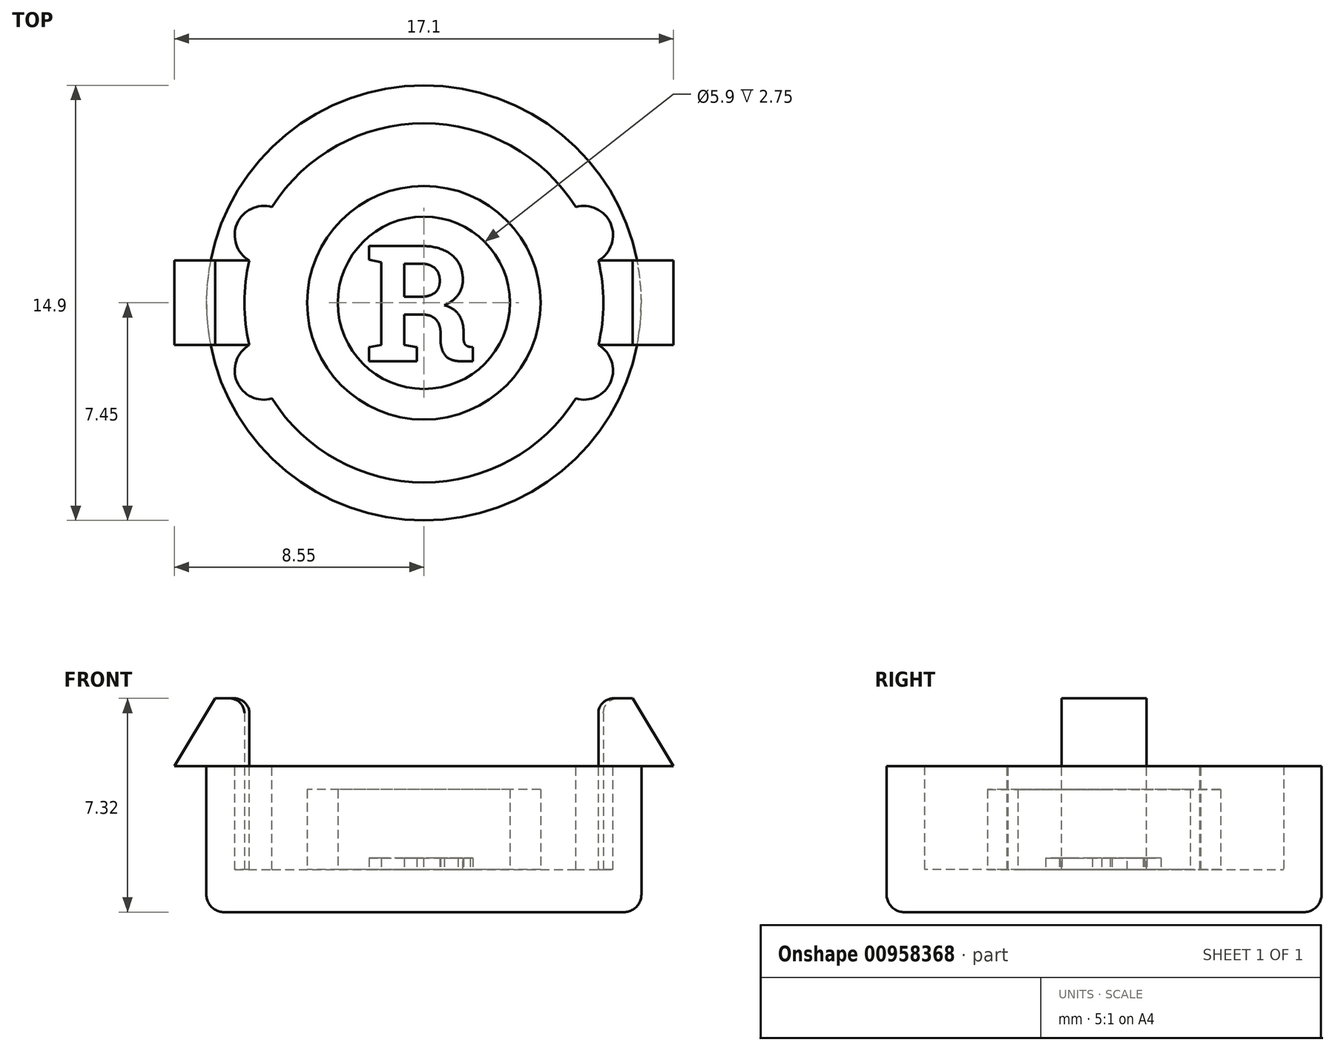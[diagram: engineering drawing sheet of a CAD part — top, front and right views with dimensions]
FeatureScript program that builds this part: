
annotation { "Feature Type Name" : "Feature", "Feature Type Description" : "" }
export const myFeature = defineFeature(function(context is Context, id is Id, definition is map)
    precondition{}
    {
        {
            var Q0;
            Q0=qCreatedBy(makeId("Top.planeOp"),FACE);
            var sketch = newSketch(context, id + "F0", { "sketchPlane" : qUnion([Q0])});
            skCircle(sketch, "E0", {"center": v(0, 0) * mm, "radius": 7.45 * mm});
            skCircle(sketch, "E1", {"center": v(0, 0) * mm, "radius": 6.15 * mm});
            skCircle(sketch, "E2", {"center": v(0, 0) * mm, "radius": 2.95 * mm});
            skCircle(sketch, "E3", {"center": v(0, 0) * mm, "radius": 4 * mm});
            skSolve(sketch);
        }
        {
            var Q0;
            Q0 = qSketchRegion(id + "F0", true);
            var Q1;
            Q1=makeQuery(id+"F0.imprint","IMPRINT",FACE,{"disambiguationData":[TD([[makeQuery(id+"F0.imprint","IMPRINT",EDGE,{"derivedFrom":sQuery(id+"F0.wireOp",EDGE,"E1")}),1.0]])]});
            var Q2;
            Q2=makeQuery(id+"F0.imprint","IMPRINT",FACE,{"disambiguationData":[TD([[makeQuery(id+"F0.imprint","IMPRINT",EDGE,{"derivedFrom":sQuery(id+"F0.wireOp",EDGE,"E2")}),-1.0]])]});
            var Q3;
            Q3=makeQuery(id+"F0.imprint","IMPRINT",FACE,{"disambiguationData":[TD([[makeQuery(id+"F0.imprint","IMPRINT",EDGE,{"derivedFrom":sQuery(id+"F0.wireOp",EDGE,"E2")}),1.0]])]});
            extrude(context, id + "F1", {"entities" : qUnion([Q0, Q1, Q2, Q3]), "depth" : 1.45 * mm, "offsetDistance" : 25 * mm});
        }
        {
            var Q0;
            Q0=makeQuery(id+"F0.imprint","IMPRINT",FACE,{"disambiguationData":[TD([[makeQuery(id+"F0.imprint","IMPRINT",EDGE,{"derivedFrom":sQuery(id+"F0.wireOp",EDGE,"E0")}),1.0]])]});
            extrude(context, id + "F2", {"entities" : qUnion([Q0]), "operationType" : NewBodyOperationType.ADD, "depth" : 5 * mm, "offsetDistance" : 25 * mm});
        }
        {
            var Q0;
            Q0=makeQuery(id+"F0.imprint","IMPRINT",FACE,{"disambiguationData":[TD([[makeQuery(id+"F0.imprint","IMPRINT",EDGE,{"derivedFrom":sQuery(id+"F0.wireOp",EDGE,"E2")}),-1.0]])]});
            var Q1;
            Q1=sQuery(id+"F0.wireOp",EDGE,"E2");
            var Q2;
            Q2=makeQuery(id+"F2.opExtrude","CAP_FACE",FACE,{"disambiguationData":[OSD([sQuery(id+"F0.wireOp",EDGE,"E0"),sQuery(id+"F0.wireOp",EDGE,"E1")])],"isStart":false});
            extrude(context, id + "F3", {"entities" : qUnion([Q0]), "operationType" : NewBodyOperationType.ADD, "surfaceEntities" : qUnion([Q1]), "endBound" : BoundingType.UP_TO_SURFACE, "depth" : 25 * mm, "endBoundEntityFace" : qUnion([Q2]), "hasOffset" : true, "offsetDistance" : 0.8 * mm});
        }
        {
            var Q0;
            Q0=qCreatedBy(makeId("Front.planeOp"),FACE);
            var sketch = newSketch(context, id + "F4", { "sketchPlane" : qUnion([Q0])});
            skLineSegment(sketch, "E4.0", {"start": v(-6.15, 5) * mm, "end": v(6.15, 5) * mm});
            skLineSegment(sketch, "E5.0", {"start": v(-7.45, 5) * mm, "end": v(7.45, 5) * mm});
            skLineSegment(sketch, "E6", {"start": v(-6.15, 5) * mm, "end": v(-6.15, 7.32) * mm});
            skLineSegment(sketch, "E7", {"start": v(-6.15, 7.32) * mm, "end": v(-7.15, 7.32) * mm});
            skLineSegment(sketch, "E8", {"start": v(-7.15, 7.32) * mm, "end": v(-8.55, 5) * mm});
            skLineSegment(sketch, "E9", {"start": v(-8.55, 5) * mm, "end": v(-7.45, 5) * mm});
            skLineSegment(sketch, "E10", {"start": v(0, 0) * mm, "end": v(0, 43.12) * mm, "construction": true});
            skLineSegment(sketch, "E11.MirrorCS", {"start": v(6.15, 5) * mm, "end": v(6.15, 7.32) * mm});
            skLineSegment(sketch, "E12.MirrorCS", {"start": v(7.15, 7.32) * mm, "end": v(8.55, 5) * mm});
            skLineSegment(sketch, "E13.MirrorCS", {"start": v(8.55, 5) * mm, "end": v(7.45, 5) * mm});
            skLineSegment(sketch, "E14.MirrorCS", {"start": v(6.15, 7.32) * mm, "end": v(7.15, 7.32) * mm});
            skLineSegment(sketch, "E15", {"start": v(-6.15, 7.32) * mm, "end": v(6.15, 7.32) * mm});
            skSolve(sketch);
        }
        {
            var Q0;
            {var subQ0=sQuery(id+"F4.wireOp",EDGE,"E6");Q0=makeQuery(id+"F4.imprint","IMPRINT",FACE,{"disambiguationData":[TD([[makeQuery(id+"F4.imprint","IMPRINT",EDGE,{"derivedFrom":subQ0}),1.0]])]});}
            var Q1;
            {var subQ1=sQuery(id+"F4.wireOp",EDGE,"E11.MirrorCS");Q1=makeQuery(id+"F4.imprint","IMPRINT",FACE,{"disambiguationData":[TD([[makeQuery(id+"F4.imprint","IMPRINT",EDGE,{"derivedFrom":subQ1}),-1.0]])]});}
            var Q2;
            {var subQ0=sQuery(id+"F4.wireOp",EDGE,"E6");Q2=makeQuery(id+"F4.imprint","IMPRINT",FACE,{"disambiguationData":[TD([[makeQuery(id+"F4.imprint","IMPRINT",EDGE,{"derivedFrom":subQ0}),-1.0]])]});}
            extrude(context, id + "F5", {"entities" : qUnion([Q0, Q1, Q2]), "operationType" : NewBodyOperationType.ADD, "endBound" : BoundingType.SYMMETRIC, "depth" : 2.9 * mm, "offsetDistance" : 25 * mm});
        }
        {
            var Q0;
            Q0=makeQuery(id+"F3.boolean.opBoolean","SPLIT",FACE,{"disambiguationData":[TD([makeQuery(id+"F2.opExtrude","SWEPT_FACE",FACE,{"disambiguationData":[OSD([sQuery(id+"F0.wireOp",EDGE,"E1")])]})])],"derivedFrom":makeQuery(id+"F1.opExtrude","CAP_FACE",FACE,{"disambiguationData":[OSD([sQuery(id+"F0.wireOp",EDGE,"E0")])],"isStart":false})});
            var Q1;
            Q1=makeQuery(id+"F3.opExtrude","CAP_FACE",FACE,{"disambiguationData":[OSD([sQuery(id+"F0.wireOp",EDGE,"E2"),sQuery(id+"F0.wireOp",EDGE,"E3")])],"isStart":false});
            var Q2;
            Q2=makeQuery(id+"F3.boolean.opBoolean","SPLIT",FACE,{"disambiguationData":[TD([makeQuery(id+"F3.opExtrude","SWEPT_FACE",FACE,{"disambiguationData":[OSD([sQuery(id+"F0.wireOp",EDGE,"E2")])]})])],"derivedFrom":makeQuery(id+"F1.opExtrude","CAP_FACE",FACE,{"disambiguationData":[OSD([sQuery(id+"F0.wireOp",EDGE,"E0")])],"isStart":false})});
            extrude(context, id + "F6", {"entities" : qUnion([Q0, Q1, Q2]), "operationType" : NewBodyOperationType.REMOVE, "endBound" : BoundingType.THROUGH_ALL, "depth" : 25 * mm, "offsetDistance" : 25 * mm});
        }
        {
            var Q0;
            {var subQ0=sQuery(id+"F0.wireOp",EDGE,"E1");var subQ1=sQuery(id+"F0.wireOp",EDGE,"E0");var subQ2=makeQuery(id+"F2.opExtrude","CAP_FACE",FACE,{"disambiguationData":[OSD([subQ1,subQ0])],"isStart":false});var subQ3=sQuery(id+"F4.wireOp",EDGE,"E9");var subQ4=sQuery(id+"F4.wireOp",EDGE,"E6");var subQ5=sQuery(id+"F4.wireOp",EDGE,"E5.0");Q0=makeQuery(id+"F5.boolean.opBoolean","SPLIT",FACE,{"disambiguationData":[TD([makeQuery(id+"F5.opExtrude","CAP_FACE",FACE,{"disambiguationData":[OSD([subQ5,subQ4,sQuery(id+"F4.wireOp",EDGE,"E7"),sQuery(id+"F4.wireOp",EDGE,"E8"),subQ3])],"isStart":true})])],"derivedFrom":subQ2});}
            var sketch = newSketch(context, id + "F7", { "sketchPlane" : qUnion([Q0])});
            skLineSegment(sketch, "E16", {"start": v(0, 0) * mm, "end": v(0, 21.63) * mm, "construction": true});
            skLineSegment(sketch, "E17", {"start": v(0, 0) * mm, "end": v(-31.97, 0) * mm, "construction": true});
            skCircle(sketch, "E18", {"center": v(-5.48, 2.32) * mm, "radius": 1 * mm});
            skCircle(sketch, "E19.MirrorC", {"center": v(-5.48, -2.32) * mm, "radius": 1 * mm});
            skCircle(sketch, "E20.MirrorC", {"center": v(5.48, 2.32) * mm, "radius": 1 * mm});
            skCircle(sketch, "E21.MirrorC", {"center": v(5.48, -2.32) * mm, "radius": 1 * mm});
            skSolve(sketch);
        }
        {
            var Q0;
            Q0 = qSketchRegion(id + "F7", true);
            var Q1;
            Q1=makeQuery(id+"F3.boolean.opBoolean","SPLIT",FACE,{"disambiguationData":[TD([makeQuery(id+"F2.opExtrude","SWEPT_FACE",FACE,{"disambiguationData":[OSD([sQuery(id+"F0.wireOp",EDGE,"E1")])]})])],"derivedFrom":makeQuery(id+"F1.opExtrude","CAP_FACE",FACE,{"disambiguationData":[OSD([sQuery(id+"F0.wireOp",EDGE,"E0")])],"isStart":false})});
            extrude(context, id + "F8", {"entities" : qUnion([Q0]), "operationType" : NewBodyOperationType.REMOVE, "endBound" : BoundingType.UP_TO_SURFACE, "oppositeDirection" : true, "depth" : 25 * mm, "endBoundEntityFace" : qUnion([Q1]), "offsetDistance" : 25 * mm});
        }
        {
            var Q0;
            Q0=makeQuery(id+"F3.boolean.opBoolean","SPLIT",FACE,{"disambiguationData":[TD([makeQuery(id+"F3.opExtrude","SWEPT_FACE",FACE,{"disambiguationData":[OSD([sQuery(id+"F0.wireOp",EDGE,"E2")])]})])],"derivedFrom":makeQuery(id+"F1.opExtrude","CAP_FACE",FACE,{"disambiguationData":[OSD([sQuery(id+"F0.wireOp",EDGE,"E0")])],"isStart":false})});
            var sketch = newSketch(context, id + "F9", { "sketchPlane" : qUnion([Q0])});
            skText(sketch, "E22", { "text": "R", "fontName": "RobotoSlab-Bold.ttf"});
            const initialGuessF9  = {"E22": [-0.00203, -0.002, 1, 0, 0.004]};
            skSetInitialGuess(sketch, initialGuessF9);
            skSolve(sketch);
        }
        {
            var Q0;
            Q0=makeQuery(id+"F9.imprint","IMPRINT",FACE,{"disambiguationData":[TD([[makeQuery(id+"F9.imprint","IMPRINT",EDGE,{"derivedFrom":sQuery(id+"F9.wireOp",EDGE,"E22.sketch_text.stroke-0")}),-1.0]])]});
            extrude(context, id + "F10", {"entities" : qUnion([Q0]), "operationType" : NewBodyOperationType.ADD, "depth" : 0.4 * mm, "offsetDistance" : 25 * mm});
        }
        {
            var Q0;
            Q0=makeQuery(id+"F1.opExtrude","CAP_FACE",FACE,{"disambiguationData":[OSD([sQuery(id+"F0.wireOp",EDGE,"E0")])],"isStart":true});
            fillet(context, id + "F11", {"entities" : qUnion([Q0]), "radius" : .6 * mm, "tangentPropagation" : true, "allowEdgeOverflow" : false});
        }
        {
            var Q0;
            Q0=makeQuery(id+"F6.boolean.opBoolean","INTERSECT",EDGE,{"disambiguationData":[OD(0.0)],"derivedFrom":[makeQuery(id+"F5.opExtrude","SWEPT_FACE",FACE,{"disambiguationData":[OSD([sQuery(id+"F4.wireOp",EDGE,"E7"),sQuery(id+"F4.wireOp",EDGE,"E14.MirrorCS"),sQuery(id+"F4.wireOp",EDGE,"E15")])]}),makeQuery(id+"F6.opExtrude","SWEPT_FACE",FACE,{"disambiguationData":[OSD([sQuery(id+"F0.wireOp",EDGE,"E0"),sQuery(id+"F0.wireOp",EDGE,"E1")])]})]});
            var Q1;
            Q1=makeQuery(id+"F6.boolean.opBoolean","INTERSECT",EDGE,{"disambiguationData":[OD(1.0)],"derivedFrom":[makeQuery(id+"F5.opExtrude","SWEPT_FACE",FACE,{"disambiguationData":[OSD([sQuery(id+"F4.wireOp",EDGE,"E7"),sQuery(id+"F4.wireOp",EDGE,"E14.MirrorCS"),sQuery(id+"F4.wireOp",EDGE,"E15")])]}),makeQuery(id+"F6.opExtrude","SWEPT_FACE",FACE,{"disambiguationData":[OSD([sQuery(id+"F0.wireOp",EDGE,"E0"),sQuery(id+"F0.wireOp",EDGE,"E1")])]})]});
            fillet(context, id + "F12", {"entities" : qUnion([Q0, Q1]), "radius" : .5 * mm, "tangentPropagation" : true, "allowEdgeOverflow" : false});
        }
    });
